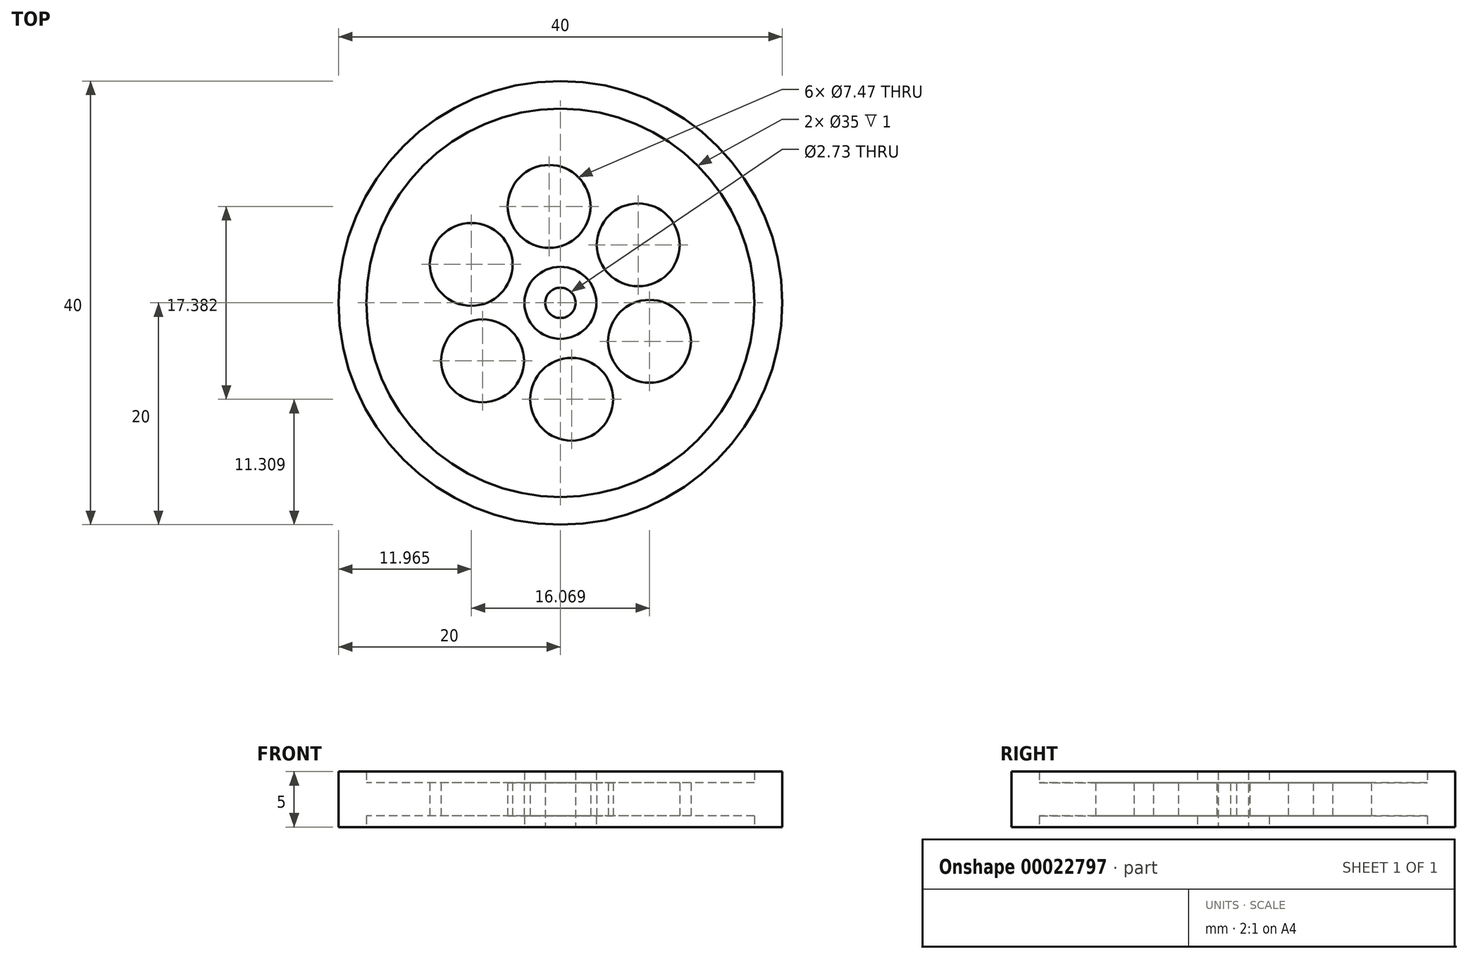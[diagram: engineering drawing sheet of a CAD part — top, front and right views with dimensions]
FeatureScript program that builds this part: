
annotation { "Feature Type Name" : "Feature", "Feature Type Description" : "" }
export const myFeature = defineFeature(function(context is Context, id is Id, definition is map)
    precondition{}
    {
        {
            var Q0;
            Q0=qCreatedBy(makeId("Top.planeOp"),FACE);
            var sketch = newSketch(context, id + "F0", { "sketchPlane" : qUnion([Q0])});
            skCircle(sketch, "E0", {"center": v(0, 0) * mm, "radius": 20 * mm});
            skCircle(sketch, "E1", {"center": v(0, 0) * mm, "radius": 17.5 * mm});
            skCircle(sketch, "E2", {"center": v(-8.03, 3.47) * mm, "radius": 3.73 * mm});
            skCircle(sketch, "E3.1.0", {"center": v(-7.02, -5.23) * mm, "radius": 3.73 * mm});
            skCircle(sketch, "E3.2.0", {"center": v(1.02, -8.7) * mm, "radius": 3.73 * mm});
            skCircle(sketch, "E3.3.0", {"center": v(8.03, -3.47) * mm, "radius": 3.73 * mm});
            skCircle(sketch, "E3.4.0", {"center": v(7.02, 5.23) * mm, "radius": 3.73 * mm});
            skCircle(sketch, "E3.5.0", {"center": v(-1.02, 8.7) * mm, "radius": 3.73 * mm});
            skPoint(sketch, "E4.orphan", {"position": v(-16.07, 6.93) * mm});
            skCircle(sketch, "E5", {"center": v(0, 0) * mm, "radius": 3.24 * mm});
            skCircle(sketch, "E6", {"center": v(0, 0) * mm, "radius": 1.37 * mm});
            skLineSegment(sketch, "E7", {"start": v(0, 0) * mm, "end": v(18.42, -7.8) * mm});
            skLineSegment(sketch, "E8", {"start": v(0, 0) * mm, "end": v(0.53, 1.26) * mm});
            skSolve(sketch);
        }
        {
            var Q0;
            Q0=makeQuery(id+"F0.imprint","IMPRINT",FACE,{"disambiguationData":[TD([[makeQuery(id+"F0.imprint","IMPRINT",EDGE,{"derivedFrom":sQuery(id+"F0.wireOp",EDGE,"E0")}),1.0]])]});
            extrude(context, id + "F1", {"entities" : qUnion([Q0]), "endBound" : BoundingType.SYMMETRIC, "depth" : 5 * mm});
        }
        {
            var Q0;
            Q0 = qSketchRegion(id + "F0", true);
            var Q1;
            Q1=makeQuery(id+"F0.imprint","IMPRINT",FACE,{"disambiguationData":[TD([[makeQuery(id+"F0.imprint","IMPRINT",EDGE,{"derivedFrom":sQuery(id+"F0.wireOp",EDGE,"E1")}),1.0]])]});
            extrude(context, id + "F2", {"entities" : qUnion([Q0, Q1]), "operationType" : NewBodyOperationType.ADD, "endBound" : BoundingType.SYMMETRIC, "depth" : 3 * mm});
        }
        {
            var Q0;
            Q0=makeQuery(id+"F0.imprint","IMPRINT",FACE,{"disambiguationData":[TD([[makeQuery(id+"F0.imprint","IMPRINT",EDGE,{"derivedFrom":sQuery(id+"F0.wireOp",EDGE,"E5")}),1.0]])]});
            extrude(context, id + "F3", {"entities" : qUnion([Q0]), "operationType" : NewBodyOperationType.ADD, "endBound" : BoundingType.SYMMETRIC, "depth" : 5 * mm});
        }
    });
